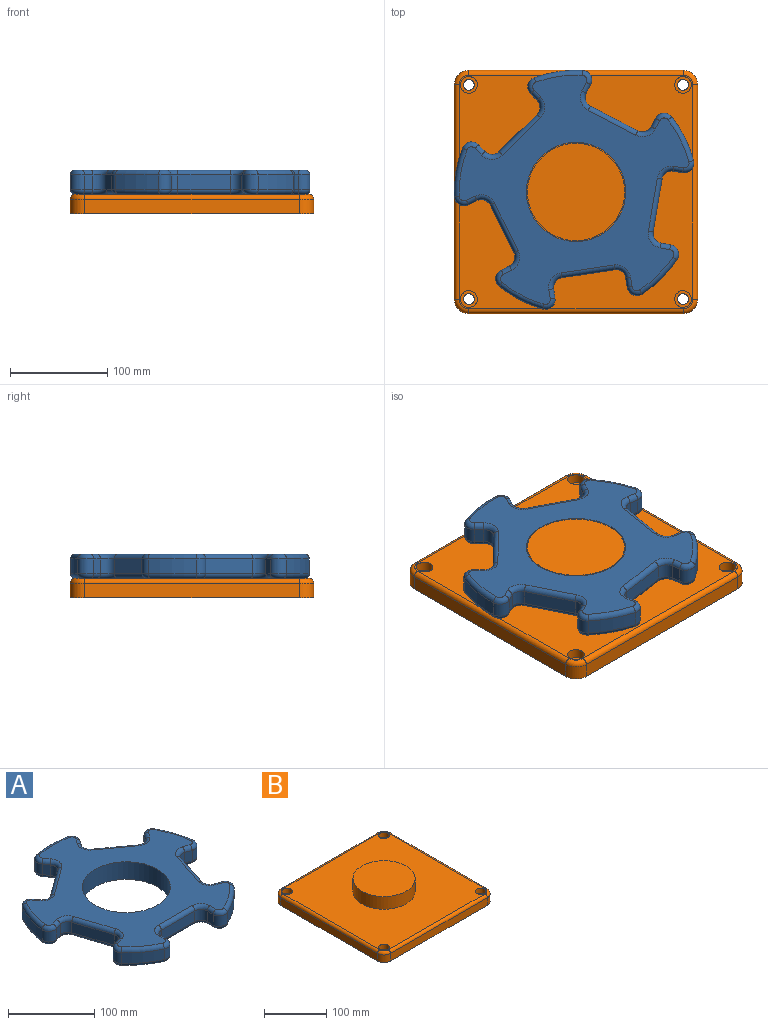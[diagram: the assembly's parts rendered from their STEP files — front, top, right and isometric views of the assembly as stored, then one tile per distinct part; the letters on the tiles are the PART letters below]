
ASSEMBLY  parts=2 mates=1
PART A: 123 faces, bbox 268.9x258.5x25 mm
  f0: plane 238.57x229.73mm, normal (0,0,1), area 21505.7mm2, adj f6,f83,f84,f85,f86,f87,f88,f89
  f1: plane 238.57x229.73mm, normal (0,0,-1), area 21505.7mm2, adj f6,f43,f44,f45,f46,f47,f48,f49
  f2: cylinder r=125mm len=47.82mm, axis (0,0,-1), area 759.5mm2, adj f34,f42,f74,f114
  f3: cylinder r=125mm len=50.29mm, axis (0,0,-1), area 759.5mm2, adj f27,f35,f75,f115
  f4: cylinder r=125mm len=47.82mm, axis (0,0,-1), area 759.5mm2, adj f20,f28,f59,f99
  f5: cylinder r=125mm len=40.68mm, axis (0,0,-1), area 759.5mm2, adj f13,f21,f43,f83
  f6: cylinder r=51mm len=102mm, axis (0,0,-1), area 8011.1mm2, adj f0,f1
  f7: cylinder r=125mm len=40.68mm, axis (0,0,-1), area 759.5mm2, adj f14,f41,f58,f98
  f8: plane 15x9.73mm, normal (-1,0,0), area 146mm2, adj f11,f14,f54,f94
  f9: plane 55x15mm, normal (0,-1,0), area 825mm2, adj f11,f12,f50,f90
  f10: plane 15x9.73mm, normal (1,0,0), area 146mm2, adj f12,f13,f46,f86
  f11: cylinder r=10mm len=15mm, axis (0,0,-1), area 235.6mm2, adj f8,f9,f52,f92
  f12: cylinder r=10mm len=15mm, axis (0,0,-1), area 235.6mm2, adj f9,f10,f48,f88
  f13: cylinder r=10mm len=15mm, axis (0,0,-1), area 299.5mm2, adj f5,f10,f44,f84
  f14: cylinder r=10mm len=15mm, axis (0,0,-1), area 299.5mm2, adj f7,f8,f56,f96
  f15: plane 15x9.26mm, normal (-0.31,0.95,0), area 146mm2, adj f18,f21,f47,f87
  f16: plane 52.31x17mm, normal (-0.95,-0.31,0), area 825mm2, adj f18,f19,f51,f91
  f17: plane 15x9.26mm, normal (0.31,-0.95,0), area 146mm2, adj f19,f20,f55,f95
  f18: cylinder r=10mm len=15mm, axis (0,0,-1), area 235.6mm2, adj f15,f16,f49,f89
  f19: cylinder r=10mm len=15mm, axis (0,0,-1), area 235.6mm2, adj f16,f17,f53,f93
  f20: cylinder r=10mm len=15mm, axis (0,0,-1), area 299.5mm2, adj f4,f17,f57,f97
  f21: cylinder r=10mm len=16.25mm, axis (0,0,-1), area 299.5mm2, adj f5,f15,f45,f85
  f22: plane 15x7.87mm, normal (0.81,0.59,0), area 146mm2, adj f25,f28,f63,f103
  f23: plane 44.5x32.33mm, normal (-0.59,0.81,0), area 825mm2, adj f25,f26,f67,f107
  f24: plane 15x7.87mm, normal (-0.81,-0.59,0), area 146mm2, adj f26,f27,f71,f111
  f25: cylinder r=10mm len=15mm, axis (0,0,-1), area 235.6mm2, adj f22,f23,f65,f105
  f26: cylinder r=10mm len=15mm, axis (0,0,-1), area 235.6mm2, adj f23,f24,f69,f109
  f27: cylinder r=10mm len=15.67mm, axis (0,0,-1), area 299.5mm2, adj f3,f24,f73,f113
  f28: cylinder r=10mm len=16.78mm, axis (0,0,-1), area 299.5mm2, adj f4,f22,f61,f101
  f29: plane 15x7.87mm, normal (0.81,-0.59,0), area 146mm2, adj f32,f35,f79,f119
  f30: plane 44.5x32.33mm, normal (0.59,0.81,0), area 825mm2, adj f32,f33,f82,f122
  f31: plane 15x7.87mm, normal (-0.81,0.59,0), area 146mm2, adj f33,f34,f78,f118
  f32: cylinder r=10mm len=15mm, axis (0,0,-1), area 235.6mm2, adj f29,f30,f81,f121
  f33: cylinder r=10mm len=15mm, axis (0,0,-1), area 235.6mm2, adj f30,f31,f80,f120
  f34: cylinder r=10mm len=16.78mm, axis (0,0,-1), area 299.5mm2, adj f2,f31,f76,f116
  f35: cylinder r=10mm len=15.67mm, axis (0,0,-1), area 299.5mm2, adj f3,f29,f77,f117
  f36: plane 15x9.26mm, normal (-0.31,-0.95,0), area 146mm2, adj f39,f42,f70,f110
  f37: plane 52.31x17mm, normal (0.95,-0.31,0), area 825mm2, adj f39,f40,f66,f106
  f38: plane 15x9.26mm, normal (0.31,0.95,0), area 146mm2, adj f40,f41,f62,f102
  f39: cylinder r=10mm len=15mm, axis (0,0,-1), area 235.6mm2, adj f36,f37,f68,f108
  f40: cylinder r=10mm len=15mm, axis (0,0,-1), area 235.6mm2, adj f37,f38,f64,f104
  f41: cylinder r=10mm len=16.25mm, axis (0,0,-1), area 299.5mm2, adj f7,f38,f60,f100
  f42: cylinder r=10mm len=15mm, axis (0,0,-1), area 299.5mm2, adj f2,f36,f72,f112
  f43: torus R=120mm, axis (0,0,1), area 391.9mm2, adj f1,f5,f44,f45
  f44: torus R=5mm, axis (0,0,1), area 128.3mm2, adj f1,f13,f43,f46
  f45: torus R=5mm, axis (0,0,1), area 128.3mm2, adj f1,f21,f43,f47
  f46: cylinder r=5mm len=9.73mm, axis (0,-1,0), area 76.4mm2, adj f1,f10,f44,f48
  f47: cylinder r=5mm len=10.8mm, axis (0.95,0.31,0), area 76.4mm2, adj f1,f15,f45,f49
  f48: torus R=15mm, axis (0,0,1), area 145.8mm2, adj f1,f12,f46,f50
  f49: torus R=15mm, axis (0,0,1), area 145.8mm2, adj f1,f18,f47,f51
  f50: cylinder r=5mm len=55mm, axis (-1,0,0), area 432mm2, adj f1,f9,f48,f52
  f51: cylinder r=5mm len=53.85mm, axis (-0.31,0.95,0), area 432mm2, adj f1,f16,f49,f53
  f52: torus R=15mm, axis (0,0,1), area 145.8mm2, adj f1,f11,f50,f54
  f53: torus R=15mm, axis (0,0,1), area 145.8mm2, adj f1,f19,f51,f55
  f54: cylinder r=5mm len=9.73mm, axis (0,1,0), area 76.4mm2, adj f1,f8,f52,f56
  f55: cylinder r=5mm len=10.8mm, axis (-0.95,-0.31,0), area 76.4mm2, adj f1,f17,f53,f57
  f56: torus R=5mm, axis (0,0,1), area 128.3mm2, adj f1,f14,f54,f58
  f57: torus R=5mm, axis (0,0,1), area 128.3mm2, adj f1,f20,f55,f59
  f58: torus R=120mm, axis (0,0,1), area 391.9mm2, adj f1,f7,f56,f60
  f59: torus R=120mm, axis (0,0,1), area 391.9mm2, adj f1,f4,f57,f61
  f60: torus R=5mm, axis (0,0,1), area 128.3mm2, adj f1,f41,f58,f62
  f61: torus R=5mm, axis (0,0,1), area 128.3mm2, adj f1,f28,f59,f63
  f62: cylinder r=5mm len=10.8mm, axis (0.95,-0.31,0), area 76.4mm2, adj f1,f38,f60,f64
  f63: cylinder r=5mm len=10.81mm, axis (0.59,-0.81,0), area 76.4mm2, adj f1,f22,f61,f65
  f64: torus R=15mm, axis (0,0,1), area 145.8mm2, adj f1,f40,f62,f66
  f65: torus R=15mm, axis (0,0,1), area 145.8mm2, adj f1,f25,f63,f67
  f66: cylinder r=5mm len=53.85mm, axis (-0.31,-0.95,0), area 432mm2, adj f1,f37,f64,f68
  f67: cylinder r=5mm len=47.44mm, axis (0.81,0.59,0), area 432mm2, adj f1,f23,f65,f69
  f68: torus R=15mm, axis (0,0,1), area 145.8mm2, adj f1,f39,f66,f70
  f69: torus R=15mm, axis (0,0,1), area 145.8mm2, adj f1,f26,f67,f71
  f70: cylinder r=5mm len=10.8mm, axis (-0.95,0.31,0), area 76.4mm2, adj f1,f36,f68,f72
  f71: cylinder r=5mm len=10.81mm, axis (-0.59,0.81,0), area 76.4mm2, adj f1,f24,f69,f73
  f72: torus R=5mm, axis (0,0,1), area 128.3mm2, adj f1,f42,f70,f74
  f73: torus R=5mm, axis (0,0,1), area 128.3mm2, adj f1,f27,f71,f75
  f74: torus R=120mm, axis (0,0,1), area 391.9mm2, adj f1,f2,f72,f76
  f75: torus R=120mm, axis (0,0,1), area 391.9mm2, adj f1,f3,f73,f77
  f76: torus R=5mm, axis (0,0,1), area 128.3mm2, adj f1,f34,f74,f78
  f77: torus R=5mm, axis (0,0,1), area 128.3mm2, adj f1,f35,f75,f79
  f78: cylinder r=5mm len=10.81mm, axis (0.59,0.81,0), area 76.4mm2, adj f1,f31,f76,f80
  f79: cylinder r=5mm len=10.81mm, axis (-0.59,-0.81,0), area 76.4mm2, adj f1,f29,f77,f81
  f80: torus R=15mm, axis (0,0,1), area 145.8mm2, adj f1,f33,f78,f82
  f81: torus R=15mm, axis (0,0,1), area 145.8mm2, adj f1,f32,f79,f82
  f82: cylinder r=5mm len=47.44mm, axis (0.81,-0.59,0), area 432mm2, adj f1,f30,f80,f81
  f83: torus R=120mm, axis (0,0,1), area 391.9mm2, adj f0,f5,f84,f85
  f84: torus R=5mm, axis (0,0,1), area 128.3mm2, adj f0,f13,f83,f86
  f85: torus R=5mm, axis (0,0,1), area 128.3mm2, adj f0,f21,f83,f87
  f86: cylinder r=5mm len=9.73mm, axis (0,1,0), area 76.4mm2, adj f0,f10,f84,f88
  f87: cylinder r=5mm len=10.8mm, axis (-0.95,-0.31,0), area 76.4mm2, adj f0,f15,f85,f89
  f88: torus R=15mm, axis (0,0,1), area 145.8mm2, adj f0,f12,f86,f90
  f89: torus R=15mm, axis (0,0,1), area 145.8mm2, adj f0,f18,f87,f91
  f90: cylinder r=5mm len=55mm, axis (1,0,0), area 432mm2, adj f0,f9,f88,f92
  f91: cylinder r=5mm len=53.85mm, axis (0.31,-0.95,0), area 432mm2, adj f0,f16,f89,f93
  f92: torus R=15mm, axis (0,0,1), area 145.8mm2, adj f0,f11,f90,f94
  f93: torus R=15mm, axis (0,0,1), area 145.8mm2, adj f0,f19,f91,f95
  f94: cylinder r=5mm len=9.73mm, axis (0,-1,0), area 76.4mm2, adj f0,f8,f92,f96
  f95: cylinder r=5mm len=10.8mm, axis (0.95,0.31,0), area 76.4mm2, adj f0,f17,f93,f97
  f96: torus R=5mm, axis (0,0,1), area 128.3mm2, adj f0,f14,f94,f98
  f97: torus R=5mm, axis (0,0,1), area 128.3mm2, adj f0,f20,f95,f99
  f98: torus R=120mm, axis (0,0,1), area 391.9mm2, adj f0,f7,f96,f100
  f99: torus R=120mm, axis (0,0,1), area 391.9mm2, adj f0,f4,f97,f101
  f100: torus R=5mm, axis (0,0,1), area 128.3mm2, adj f0,f41,f98,f102
  f101: torus R=5mm, axis (0,0,1), area 128.3mm2, adj f0,f28,f99,f103
  f102: cylinder r=5mm len=10.8mm, axis (-0.95,0.31,0), area 76.4mm2, adj f0,f38,f100,f104
  f103: cylinder r=5mm len=10.81mm, axis (-0.59,0.81,0), area 76.4mm2, adj f0,f22,f101,f105
  f104: torus R=15mm, axis (0,0,1), area 145.8mm2, adj f0,f40,f102,f106
  f105: torus R=15mm, axis (0,0,1), area 145.8mm2, adj f0,f25,f103,f107
  f106: cylinder r=5mm len=53.85mm, axis (0.31,0.95,0), area 432mm2, adj f0,f37,f104,f108
  f107: cylinder r=5mm len=47.44mm, axis (-0.81,-0.59,0), area 432mm2, adj f0,f23,f105,f109
  f108: torus R=15mm, axis (0,0,1), area 145.8mm2, adj f0,f39,f106,f110
  f109: torus R=15mm, axis (0,0,1), area 145.8mm2, adj f0,f26,f107,f111
  f110: cylinder r=5mm len=10.8mm, axis (0.95,-0.31,0), area 76.4mm2, adj f0,f36,f108,f112
  f111: cylinder r=5mm len=10.81mm, axis (0.59,-0.81,0), area 76.4mm2, adj f0,f24,f109,f113
  f112: torus R=5mm, axis (0,0,1), area 128.3mm2, adj f0,f42,f110,f114
  f113: torus R=5mm, axis (0,0,1), area 128.3mm2, adj f0,f27,f111,f115
  f114: torus R=120mm, axis (0,0,1), area 391.9mm2, adj f0,f2,f112,f116
  f115: torus R=120mm, axis (0,0,1), area 391.9mm2, adj f0,f3,f113,f117
  f116: torus R=5mm, axis (0,0,1), area 128.3mm2, adj f0,f34,f114,f118
  f117: torus R=5mm, axis (0,0,1), area 128.3mm2, adj f0,f35,f115,f119
  f118: cylinder r=5mm len=10.81mm, axis (-0.59,-0.81,0), area 76.4mm2, adj f0,f31,f116,f120
  f119: cylinder r=5mm len=10.81mm, axis (0.59,0.81,0), area 76.4mm2, adj f0,f29,f117,f121
  f120: torus R=15mm, axis (0,0,1), area 145.8mm2, adj f0,f33,f118,f122
  f121: torus R=15mm, axis (0,0,1), area 145.8mm2, adj f0,f32,f119,f122
  f122: cylinder r=5mm len=47.44mm, axis (-0.81,0.59,0), area 432mm2, adj f0,f30,f120,f121
PART B: 32 faces, bbox 252.5x252.5x45 mm
  f0: plane 220x15mm, normal (1,0,0), area 3300mm2, adj f5,f8,f11,f27
  f1: plane 220x15mm, normal (0,1,0), area 3300mm2, adj f5,f8,f9,f31
  f2: plane 220x15mm, normal (-1,0,0), area 3300mm2, adj f5,f9,f10,f28
  f3: plane 220x15mm, normal (0,-1,0), area 3300mm2, adj f5,f10,f11,f24
  f4: plane 240x240mm, normal (0,0,1), area 48725.4mm2, adj f6,f14,f17,f20,f23,f24,f25,f26
  f5: plane 250x250mm, normal (0,0,-1), area 61926.7mm2, adj f0,f1,f2,f3,f8,f9,f10,f11
  f6: cylinder r=50mm len=100mm, axis (0,0,-1), area 7854mm2, adj f4,f7
  f7: plane 100x100mm, normal (0,0,1), area 7854mm2, adj f6
  f8: cylinder r=15mm len=15mm, axis (0,0,-1), area 353.4mm2, adj f0,f1,f5,f29
  f9: cylinder r=15mm len=15mm, axis (0,0,1), area 353.4mm2, adj f1,f2,f5,f30
  f10: cylinder r=15mm len=15mm, axis (0,0,-1), area 353.4mm2, adj f2,f3,f5,f26
  f11: cylinder r=15mm len=15mm, axis (0,0,1), area 353.4mm2, adj f0,f3,f5,f25
  f12: cylinder r=5.5mm len=11mm, axis (0,0,1), area 345.6mm2, adj f5,f13
  f13: plane 17.25x17.25mm, normal (0,0,1), area 138.7mm2, adj f12,f14
  f14: cylinder r=8.62mm len=17.25mm, axis (0,0,1), area 541.9mm2, adj f4,f13
  f15: cylinder r=5.5mm len=11mm, axis (0,0,1), area 345.6mm2, adj f5,f16
  f16: plane 17.25x17.25mm, normal (0,0,1), area 138.7mm2, adj f15,f17
  f17: cylinder r=8.62mm len=17.25mm, axis (0,0,1), area 541.9mm2, adj f4,f16
  f18: cylinder r=5.5mm len=11mm, axis (0,0,1), area 345.6mm2, adj f5,f19
  f19: plane 17.25x17.25mm, normal (0,0,1), area 138.7mm2, adj f18,f20
  f20: cylinder r=8.62mm len=17.25mm, axis (0,0,1), area 541.9mm2, adj f4,f19
  f21: cylinder r=5.5mm len=11mm, axis (0,0,1), area 345.6mm2, adj f5,f22
  f22: plane 17.25x17.25mm, normal (0,0,1), area 138.7mm2, adj f21,f23
  f23: cylinder r=8.62mm len=17.25mm, axis (0,0,1), area 541.9mm2, adj f4,f22
  f24: cylinder r=5mm len=220mm, axis (-1,0,0), area 1727.9mm2, adj f3,f4,f25,f26
  f25: torus R=10mm, axis (0,0,1), area 162.6mm2, adj f4,f11,f24,f27
  f26: torus R=10mm, axis (0,0,1), area 162.6mm2, adj f4,f10,f24,f28
  f27: cylinder r=5mm len=220mm, axis (0,-1,0), area 1727.9mm2, adj f0,f4,f25,f29
  f28: cylinder r=5mm len=220mm, axis (0,1,0), area 1727.9mm2, adj f2,f4,f26,f30
  f29: torus R=10mm, axis (0,0,1), area 162.6mm2, adj f4,f8,f27,f31
  f30: torus R=10mm, axis (0,0,1), area 162.6mm2, adj f4,f9,f28,f31
  f31: cylinder r=5mm len=220mm, axis (1,0,0), area 1727.9mm2, adj f1,f4,f29,f30
PLACE A rot(axis=(0,0,-1),63.5deg) t=(0,0,0)mm
PLACE B at identity fixed
MATE revolute B.f6 <-> A.f2  axis (0,0,1) through (0,0,20)mm
